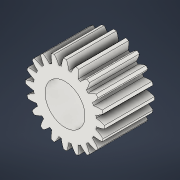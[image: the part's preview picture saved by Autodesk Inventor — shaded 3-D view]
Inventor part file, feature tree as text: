
AUTODESK INVENTOR PART (.ipt)
format: ipt  version: 2021 (Build 250183000, 183)  size: 274,432 bytes
history: native  units: mm (DEFAULTED — no unit token found)
features: plane x3, other x3, sketch x3, extrude x2
ambient origin geometry x8: Origin, YZ Plane, XZ Plane, XY Plane, X Axis, Y Axis, Z Axis, Center Point
bodies: Solid1 (feature_tree)
feature tree (11):
  extrude  "Extrusion1"  Depth=1.25mm TaperAngle=0.0deg
  plane  "Work Plane2"
  plane  "Work Plane8"
  plane  "Work Plane9"
  other  "Engrenagem reta"
  extrude  "Extrusão2"  Depth=10.0mm TaperAngle=0.0deg
  sketch  "Sketch1"  dims[d0=1.979988mm d1=1.25mm d2=0.0mm]
  sketch  "Sketch2"  dims[d3=1.8mm d4=10.0mm d5=0.0mm]
  other  "Srf1"
  sketch  "Esboço3"  dims[d16=3.597588mm d17=0.0mm d34=1.570796mm d39=0.0mm d41=0.0mm d43=3.597588mm d46=3.597588mm d47=0.0mm d48=0.0mm d49=1.0mm d50=1.25mm d51=0.0mm]
  other  "Diâmetro do flanco"
